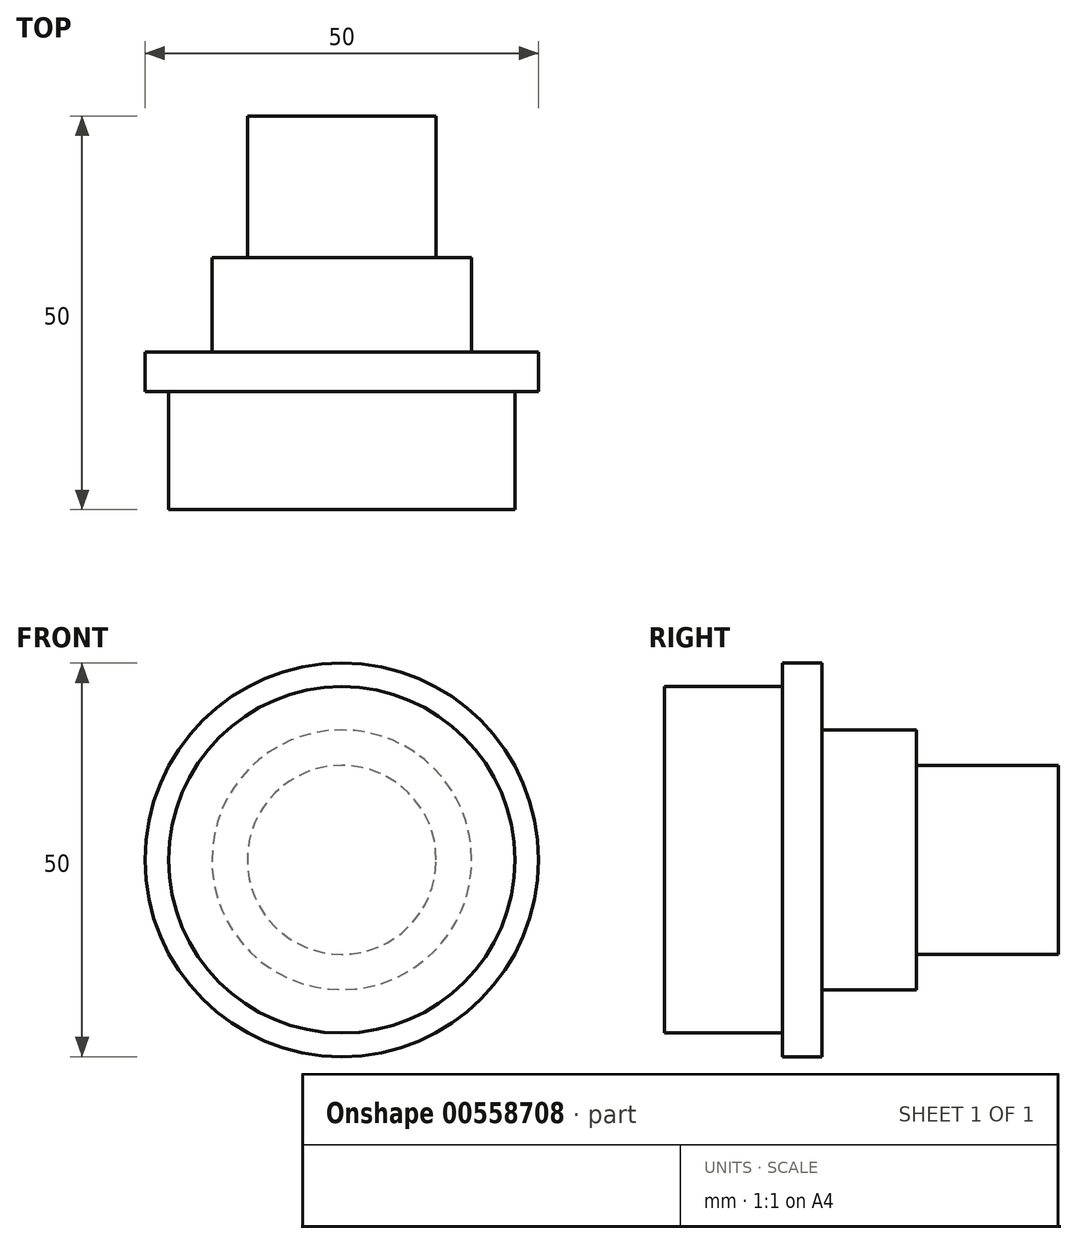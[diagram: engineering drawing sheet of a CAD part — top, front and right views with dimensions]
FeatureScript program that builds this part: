
annotation { "Feature Type Name" : "Feature", "Feature Type Description" : "" }
export const myFeature = defineFeature(function(context is Context, id is Id, definition is map)
    precondition{}
    {
        {
            var Q0;
            Q0=qCreatedBy(makeId("Right.planeOp"),FACE);
            var sketch = newSketch(context, id + "F0", { "sketchPlane" : qUnion([Q0])});
            skLineSegment(sketch, "E0", {"start": v(-50, 0) * mm, "end": v(-50, 22) * mm});
            skLineSegment(sketch, "E1", {"start": v(-50, 22) * mm, "end": v(-35, 22) * mm});
            skLineSegment(sketch, "E2", {"start": v(-35, 22) * mm, "end": v(-35, 25) * mm});
            skLineSegment(sketch, "E3", {"start": v(-35, 25) * mm, "end": v(-30, 25) * mm});
            skLineSegment(sketch, "E4", {"start": v(-30, 25) * mm, "end": v(-30, 16.5) * mm});
            skLineSegment(sketch, "E5", {"start": v(-30, 16.5) * mm, "end": v(-18, 16.5) * mm});
            skLineSegment(sketch, "E6", {"start": v(-18, 16.5) * mm, "end": v(-18, 12) * mm});
            skLineSegment(sketch, "E7", {"start": v(-18, 12) * mm, "end": v(0, 12) * mm});
            skLineSegment(sketch, "E8", {"start": v(0, 12) * mm, "end": v(0, 0) * mm});
            skLineSegment(sketch, "E9", {"start": v(0, 0) * mm, "end": v(-50, 0) * mm});
            skLineSegment(sketch, "E10", {"start": v(-38.19, 0) * mm, "end": v(39.44, 0) * mm, "construction": true});
            skSolve(sketch);
        }
        {
            var Q0;
            Q0=makeQuery(id+"F0.imprint","IMPRINT",FACE,{"disambiguationData":[TD([[makeQuery(id+"F0.imprint","IMPRINT",EDGE,{"derivedFrom":sQuery(id+"F0.wireOp",EDGE,"E0")}),-1.0]])]});
            var Q1;
            Q1=sQuery(id+"F0.wireOp",EDGE,"E9");
            revolve(context, id + "F1", {"entities" : qUnion([Q0]), "axis" : qUnion([Q1]), "revolveType" : RevolveType.FULL});
        }
    });
